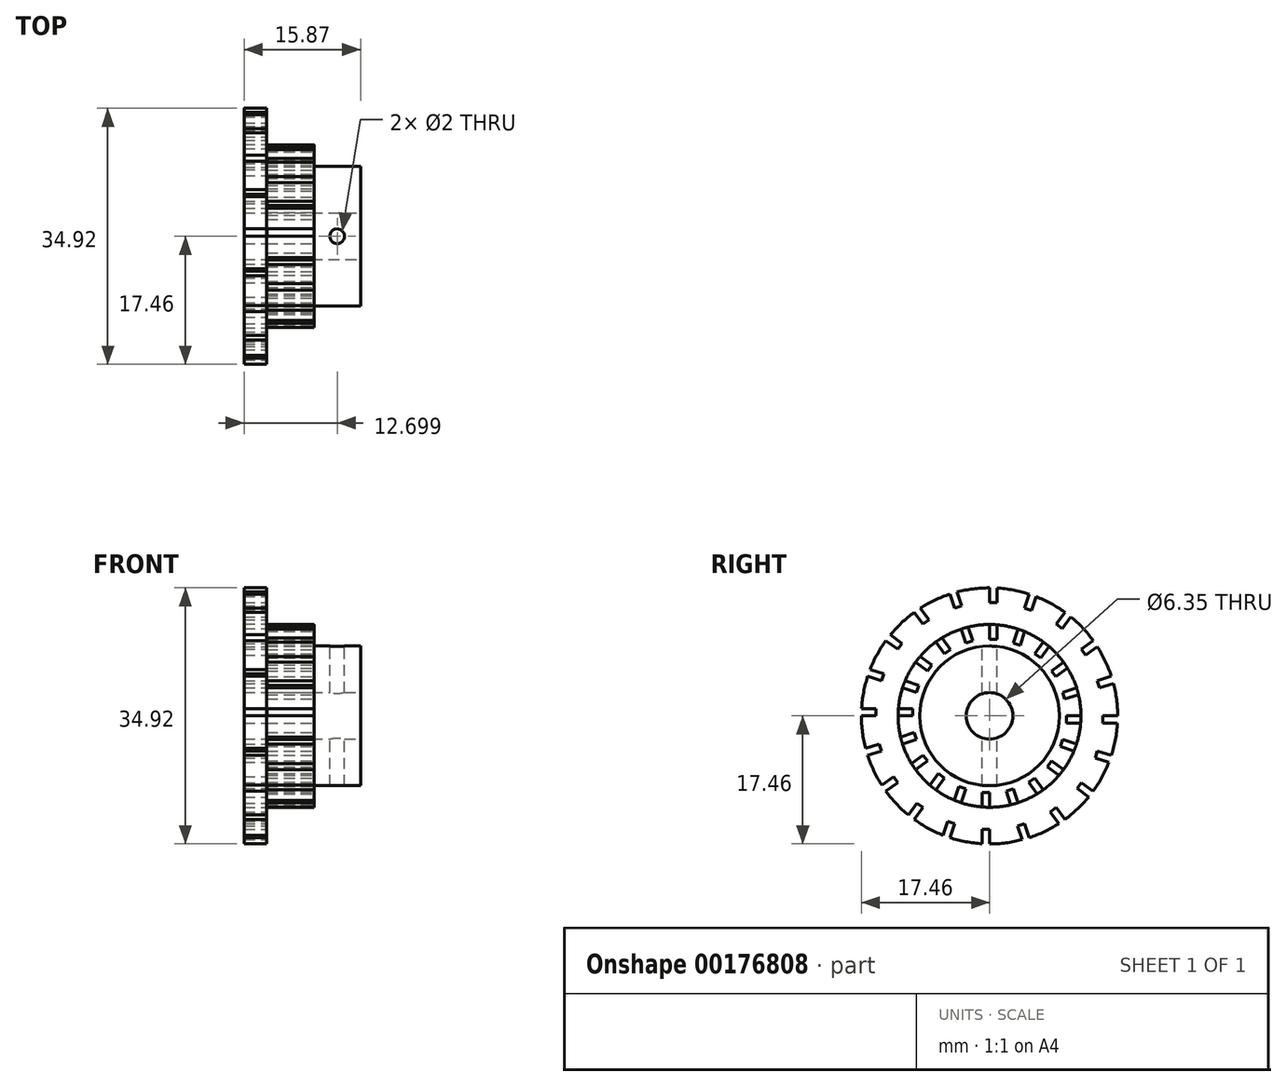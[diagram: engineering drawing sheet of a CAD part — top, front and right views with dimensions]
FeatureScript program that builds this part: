
annotation { "Feature Type Name" : "Feature", "Feature Type Description" : "" }
export const myFeature = defineFeature(function(context is Context, id is Id, definition is map)
    precondition{}
    {
        {
            var Q0;
            Q0=qCreatedBy(makeId("Front.planeOp"),FACE);
            var sketch = newSketch(context, id + "F0", { "sketchPlane" : qUnion([Q0])});
            skLineSegment(sketch, "E0", {"start": v(13.74, 3.18) * mm, "end": v(13.74, 9.53) * mm});
            skLineSegment(sketch, "E1", {"start": v(13.74, 9.53) * mm, "end": v(7.4, 9.53) * mm});
            skLineSegment(sketch, "E2", {"start": v(7.4, 9.53) * mm, "end": v(7.4, 17.46) * mm});
            skLineSegment(sketch, "E3", {"start": v(7.4, 17.46) * mm, "end": v(-2.13, 17.46) * mm});
            skLineSegment(sketch, "E4", {"start": v(-2.13, 17.46) * mm, "end": v(-2.13, 3.18) * mm});
            skLineSegment(sketch, "E5", {"start": v(-2.13, 3.18) * mm, "end": v(13.74, 3.18) * mm});
            skLineSegment(sketch, "E6", {"start": v(4.12, 0) * mm, "end": v(-4.41, 0) * mm, "construction": true});
            skSolve(sketch);
        }
        {
            var Q0;
            Q0=qSketchRegion(id+"F0",true);
            var Q1;
            Q1=sQuery(id+"F0.wireOp",EDGE,"E6");
            revolve(context, id + "F1", {"entities" : qUnion([Q0]), "axis" : qUnion([Q1]), "revolveType" : RevolveType.FULL});
        }
        {
            var Q0;
            Q0=qCreatedBy(makeId("Top.planeOp"),FACE);
            var sketch = newSketch(context, id + "F2", { "sketchPlane" : qUnion([Q0])});
            skLineSegment(sketch, "E7", {"start": v(-2.13, 17.46) * mm, "end": v(7.4, 17.46) * mm});
            skLineSegment(sketch, "E8.0", {"start": v(-2.13, 17.46) * mm, "end": v(-2.13, -17.46) * mm});
            skLineSegment(sketch, "E9.0", {"start": v(7.4, 17.46) * mm, "end": v(7.4, -17.46) * mm});
            skLineSegment(sketch, "E10", {"start": v(0.93, 17.46) * mm, "end": v(0.93, 12.46) * mm});
            skLineSegment(sketch, "E11", {"start": v(0.93, 12.46) * mm, "end": v(7.4, 12.46) * mm});
            skLineSegment(sketch, "E12", {"start": v(7.4, 12.46) * mm, "end": v(7.4, 17.46) * mm});
            skSolve(sketch);
        }
        {
            var Q0;
            Q0=qCreatedBy(makeId("Top.planeOp"),FACE);
            var sketch = newSketch(context, id + "F3", { "sketchPlane" : qUnion([Q0])});
            skLineSegment(sketch, "E13", {"start": v(-2.48, 0) * mm, "end": v(7.78, 0) * mm});
            skSolve(sketch);
        }
        {
            var Q0;
            Q0 = qSketchRegion(id + "F2", true);
            var Q1;
            Q1=sQuery(id+"F3.wireOp",EDGE,"E13");
            revolve(context, id + "F4", {"operationType" : NewBodyOperationType.REMOVE, "entities" : qUnion([Q0]), "axis" : qUnion([Q1]), "revolveType" : RevolveType.FULL, "oppositeDirection" : true});
        }
        {
            var Q0;
            Q0=makeQuery(id+"F4.boolean.opBoolean","COPY",FACE,{"derivedFrom":makeQuery(id+"F4.opRevolve","SWEPT_FACE",FACE,{"disambiguationData":[OSD([sQuery(id+"F2.wireOp",EDGE,"E10")])]})});
            var sketch = newSketch(context, id + "F5", { "sketchPlane" : qUnion([Q0])});
            skLineSegment(sketch, "E14", {"start": v(0, 18.01) * mm, "end": v(0, 15.46) * mm});
            skLineSegment(sketch, "E15", {"start": v(0, 15.46) * mm, "end": v(1, 15.46) * mm});
            skLineSegment(sketch, "E16", {"start": v(1, 15.46) * mm, "end": v(1, 18.04) * mm});
            skLineSegment(sketch, "E17", {"start": v(1, 18.04) * mm, "end": v(0, 18.01) * mm});
            skLineSegment(sketch, "E18.1.0", {"start": v(-4.62, 17.46) * mm, "end": v(-5.57, 17.13) * mm});
            skLineSegment(sketch, "E18.1.1", {"start": v(-3.83, 15.01) * mm, "end": v(-4.62, 17.46) * mm});
            skLineSegment(sketch, "E18.1.2", {"start": v(-5.57, 17.13) * mm, "end": v(-4.78, 14.7) * mm});
            skLineSegment(sketch, "E18.1.3", {"start": v(-4.78, 14.7) * mm, "end": v(-3.83, 15.01) * mm});
            skLineSegment(sketch, "E18.2.0", {"start": v(-9.8, 15.18) * mm, "end": v(-10.59, 14.57) * mm});
            skLineSegment(sketch, "E18.2.1", {"start": v(-8.28, 13.1) * mm, "end": v(-9.8, 15.18) * mm});
            skLineSegment(sketch, "E18.2.2", {"start": v(-10.59, 14.57) * mm, "end": v(-9.09, 12.5) * mm});
            skLineSegment(sketch, "E18.2.3", {"start": v(-9.09, 12.5) * mm, "end": v(-8.28, 13.1) * mm});
            skLineSegment(sketch, "E18.3.0", {"start": v(-14, 11.41) * mm, "end": v(-14.57, 10.59) * mm});
            skLineSegment(sketch, "E18.3.1", {"start": v(-11.92, 9.9) * mm, "end": v(-14, 11.41) * mm});
            skLineSegment(sketch, "E18.3.2", {"start": v(-14.57, 10.59) * mm, "end": v(-12.5, 9.09) * mm});
            skLineSegment(sketch, "E18.3.3", {"start": v(-12.5, 9.09) * mm, "end": v(-11.92, 9.9) * mm});
            skLineSegment(sketch, "E18.4.0", {"start": v(-16.84, 6.52) * mm, "end": v(-17.13, 5.57) * mm});
            skLineSegment(sketch, "E18.4.1", {"start": v(-14.4, 5.73) * mm, "end": v(-16.84, 6.52) * mm});
            skLineSegment(sketch, "E18.4.2", {"start": v(-17.13, 5.57) * mm, "end": v(-14.7, 4.78) * mm});
            skLineSegment(sketch, "E18.4.3", {"start": v(-14.7, 4.78) * mm, "end": v(-14.4, 5.73) * mm});
            skLineSegment(sketch, "E18.5.0", {"start": v(-18.04, 1) * mm, "end": v(-18.01, 0) * mm});
            skLineSegment(sketch, "E18.5.1", {"start": v(-15.46, 1) * mm, "end": v(-18.04, 1) * mm});
            skLineSegment(sketch, "E18.5.2", {"start": v(-18.01, 0) * mm, "end": v(-15.46, 0) * mm});
            skLineSegment(sketch, "E18.5.3", {"start": v(-15.46, 0) * mm, "end": v(-15.46, 1) * mm});
            skLineSegment(sketch, "E18.6.0", {"start": v(-17.46, -4.62) * mm, "end": v(-17.13, -5.57) * mm});
            skLineSegment(sketch, "E18.6.1", {"start": v(-15.01, -3.83) * mm, "end": v(-17.46, -4.62) * mm});
            skLineSegment(sketch, "E18.6.2", {"start": v(-17.13, -5.57) * mm, "end": v(-14.7, -4.78) * mm});
            skLineSegment(sketch, "E18.6.3", {"start": v(-14.7, -4.78) * mm, "end": v(-15.01, -3.83) * mm});
            skLineSegment(sketch, "E18.7.0", {"start": v(-15.18, -9.8) * mm, "end": v(-14.57, -10.59) * mm});
            skLineSegment(sketch, "E18.7.1", {"start": v(-13.1, -8.28) * mm, "end": v(-15.18, -9.8) * mm});
            skLineSegment(sketch, "E18.7.2", {"start": v(-14.57, -10.59) * mm, "end": v(-12.5, -9.09) * mm});
            skLineSegment(sketch, "E18.7.3", {"start": v(-12.5, -9.09) * mm, "end": v(-13.1, -8.28) * mm});
            skLineSegment(sketch, "E18.8.0", {"start": v(-11.41, -14) * mm, "end": v(-10.59, -14.57) * mm});
            skLineSegment(sketch, "E18.8.1", {"start": v(-9.9, -11.92) * mm, "end": v(-11.41, -14) * mm});
            skLineSegment(sketch, "E18.8.2", {"start": v(-10.59, -14.57) * mm, "end": v(-9.09, -12.5) * mm});
            skLineSegment(sketch, "E18.8.3", {"start": v(-9.09, -12.5) * mm, "end": v(-9.9, -11.92) * mm});
            skLineSegment(sketch, "E18.9.0", {"start": v(-6.52, -16.84) * mm, "end": v(-5.57, -17.13) * mm});
            skLineSegment(sketch, "E18.9.1", {"start": v(-5.73, -14.4) * mm, "end": v(-6.52, -16.84) * mm});
            skLineSegment(sketch, "E18.9.2", {"start": v(-5.57, -17.13) * mm, "end": v(-4.78, -14.7) * mm});
            skLineSegment(sketch, "E18.9.3", {"start": v(-4.78, -14.7) * mm, "end": v(-5.73, -14.4) * mm});
            skLineSegment(sketch, "E18.10.0", {"start": v(-1, -18.04) * mm, "end": v(0, -18.01) * mm});
            skLineSegment(sketch, "E18.10.1", {"start": v(-1, -15.46) * mm, "end": v(-1, -18.04) * mm});
            skLineSegment(sketch, "E18.10.2", {"start": v(0, -18.01) * mm, "end": v(0, -15.46) * mm});
            skLineSegment(sketch, "E18.10.3", {"start": v(0, -15.46) * mm, "end": v(-1, -15.46) * mm});
            skLineSegment(sketch, "E18.11.0", {"start": v(4.62, -17.46) * mm, "end": v(5.57, -17.13) * mm});
            skLineSegment(sketch, "E18.11.1", {"start": v(3.83, -15.01) * mm, "end": v(4.62, -17.46) * mm});
            skLineSegment(sketch, "E18.11.2", {"start": v(5.57, -17.13) * mm, "end": v(4.78, -14.7) * mm});
            skLineSegment(sketch, "E18.11.3", {"start": v(4.78, -14.7) * mm, "end": v(3.83, -15.01) * mm});
            skLineSegment(sketch, "E18.12.0", {"start": v(9.8, -15.18) * mm, "end": v(10.59, -14.57) * mm});
            skLineSegment(sketch, "E18.12.1", {"start": v(8.28, -13.1) * mm, "end": v(9.8, -15.18) * mm});
            skLineSegment(sketch, "E18.12.2", {"start": v(10.59, -14.57) * mm, "end": v(9.09, -12.5) * mm});
            skLineSegment(sketch, "E18.12.3", {"start": v(9.09, -12.5) * mm, "end": v(8.28, -13.1) * mm});
            skLineSegment(sketch, "E18.13.0", {"start": v(14, -11.41) * mm, "end": v(14.57, -10.59) * mm});
            skLineSegment(sketch, "E18.13.1", {"start": v(11.92, -9.9) * mm, "end": v(14, -11.41) * mm});
            skLineSegment(sketch, "E18.13.2", {"start": v(14.57, -10.59) * mm, "end": v(12.5, -9.09) * mm});
            skLineSegment(sketch, "E18.13.3", {"start": v(12.5, -9.09) * mm, "end": v(11.92, -9.9) * mm});
            skLineSegment(sketch, "E18.14.0", {"start": v(16.84, -6.52) * mm, "end": v(17.13, -5.57) * mm});
            skLineSegment(sketch, "E18.14.1", {"start": v(14.4, -5.73) * mm, "end": v(16.84, -6.52) * mm});
            skLineSegment(sketch, "E18.14.2", {"start": v(17.13, -5.57) * mm, "end": v(14.7, -4.78) * mm});
            skLineSegment(sketch, "E18.14.3", {"start": v(14.7, -4.78) * mm, "end": v(14.4, -5.73) * mm});
            skLineSegment(sketch, "E18.15.0", {"start": v(18.04, -1) * mm, "end": v(18.01, 0) * mm});
            skLineSegment(sketch, "E18.15.1", {"start": v(15.46, -1) * mm, "end": v(18.04, -1) * mm});
            skLineSegment(sketch, "E18.15.2", {"start": v(18.01, 0) * mm, "end": v(15.46, 0) * mm});
            skLineSegment(sketch, "E18.15.3", {"start": v(15.46, 0) * mm, "end": v(15.46, -1) * mm});
            skLineSegment(sketch, "E18.16.0", {"start": v(17.46, 4.62) * mm, "end": v(17.13, 5.57) * mm});
            skLineSegment(sketch, "E18.16.1", {"start": v(15.01, 3.83) * mm, "end": v(17.46, 4.62) * mm});
            skLineSegment(sketch, "E18.16.2", {"start": v(17.13, 5.57) * mm, "end": v(14.7, 4.78) * mm});
            skLineSegment(sketch, "E18.16.3", {"start": v(14.7, 4.78) * mm, "end": v(15.01, 3.83) * mm});
            skLineSegment(sketch, "E18.17.0", {"start": v(15.18, 9.8) * mm, "end": v(14.57, 10.59) * mm});
            skLineSegment(sketch, "E18.17.1", {"start": v(13.1, 8.28) * mm, "end": v(15.18, 9.8) * mm});
            skLineSegment(sketch, "E18.17.2", {"start": v(14.57, 10.59) * mm, "end": v(12.5, 9.09) * mm});
            skLineSegment(sketch, "E18.17.3", {"start": v(12.5, 9.09) * mm, "end": v(13.1, 8.28) * mm});
            skLineSegment(sketch, "E18.18.0", {"start": v(11.41, 14) * mm, "end": v(10.59, 14.57) * mm});
            skLineSegment(sketch, "E18.18.1", {"start": v(9.9, 11.92) * mm, "end": v(11.41, 14) * mm});
            skLineSegment(sketch, "E18.18.2", {"start": v(10.59, 14.57) * mm, "end": v(9.09, 12.5) * mm});
            skLineSegment(sketch, "E18.18.3", {"start": v(9.09, 12.5) * mm, "end": v(9.9, 11.92) * mm});
            skLineSegment(sketch, "E18.19.0", {"start": v(6.52, 16.84) * mm, "end": v(5.57, 17.13) * mm});
            skLineSegment(sketch, "E18.19.1", {"start": v(5.73, 14.4) * mm, "end": v(6.52, 16.84) * mm});
            skLineSegment(sketch, "E18.19.2", {"start": v(5.57, 17.13) * mm, "end": v(4.78, 14.7) * mm});
            skLineSegment(sketch, "E18.19.3", {"start": v(4.78, 14.7) * mm, "end": v(5.73, 14.4) * mm});
            skPoint(sketch, "E18.center", {"position": v(0, 0) * mm});
            skSolve(sketch);
        }
        {
            var Q0;
            Q0 = qSketchRegion(id + "F5", true);
            extrude(context, id + "F6", {"entities" : qUnion([Q0]), "operationType" : NewBodyOperationType.REMOVE, "oppositeDirection" : true, "depth" : 25 * mm});
        }
        {
            var Q0;
            Q0=makeQuery(id+"F1.opRevolve","SWEPT_FACE",FACE,{"disambiguationData":[OSD([sQuery(id+"F0.wireOp",EDGE,"E2")])]});
            var sketch = newSketch(context, id + "F7", { "sketchPlane" : qUnion([Q0])});
            skLineSegment(sketch, "E19", {"start": v(0, 12.86) * mm, "end": v(0, 10.46) * mm});
            skLineSegment(sketch, "E20", {"start": v(0, 10.46) * mm, "end": v(1, 10.46) * mm});
            skLineSegment(sketch, "E21", {"start": v(1, 10.46) * mm, "end": v(1, 12.93) * mm});
            skLineSegment(sketch, "E22", {"start": v(1, 12.93) * mm, "end": v(0, 12.86) * mm});
            skLineSegment(sketch, "E23.1.0", {"start": v(-3.05, 12.6) * mm, "end": v(-3.97, 12.23) * mm});
            skLineSegment(sketch, "E23.1.1", {"start": v(-2.28, 10.26) * mm, "end": v(-3.05, 12.6) * mm});
            skLineSegment(sketch, "E23.1.2", {"start": v(-3.97, 12.23) * mm, "end": v(-3.23, 9.95) * mm});
            skLineSegment(sketch, "E23.1.3", {"start": v(-3.23, 9.95) * mm, "end": v(-2.28, 10.26) * mm});
            skLineSegment(sketch, "E23.2.0", {"start": v(-6.8, 11.05) * mm, "end": v(-7.56, 10.4) * mm});
            skLineSegment(sketch, "E23.2.1", {"start": v(-5.34, 9.05) * mm, "end": v(-6.8, 11.05) * mm});
            skLineSegment(sketch, "E23.2.2", {"start": v(-7.56, 10.4) * mm, "end": v(-6.15, 8.46) * mm});
            skLineSegment(sketch, "E23.2.3", {"start": v(-6.15, 8.46) * mm, "end": v(-5.34, 9.05) * mm});
            skPoint(sketch, "E23.center", {"position": v(0, 0) * mm});
            skLineSegment(sketch, "E24.2.3.0", {"start": v(-9.88, 8.41) * mm, "end": v(-10.4, 7.56) * mm});
            skLineSegment(sketch, "E24.3.3.0", {"start": v(-7.88, 6.96) * mm, "end": v(-9.88, 8.41) * mm});
            skLineSegment(sketch, "E24.6.3.0", {"start": v(-10.4, 7.56) * mm, "end": v(-8.46, 6.15) * mm});
            skLineSegment(sketch, "E24.9.3.0", {"start": v(-8.46, 6.15) * mm, "end": v(-7.88, 6.96) * mm});
            skLineSegment(sketch, "E24.2.4.0", {"start": v(-12, 4.95) * mm, "end": v(-12.23, 3.97) * mm});
            skLineSegment(sketch, "E24.3.4.0", {"start": v(-9.64, 4.18) * mm, "end": v(-12, 4.95) * mm});
            skLineSegment(sketch, "E24.6.4.0", {"start": v(-12.23, 3.97) * mm, "end": v(-9.95, 3.23) * mm});
            skLineSegment(sketch, "E24.9.4.0", {"start": v(-9.95, 3.23) * mm, "end": v(-9.64, 4.18) * mm});
            skLineSegment(sketch, "E24.2.5.0", {"start": v(-12.93, 1) * mm, "end": v(-12.86, 0) * mm});
            skLineSegment(sketch, "E24.3.5.0", {"start": v(-10.46, 1) * mm, "end": v(-12.93, 1) * mm});
            skLineSegment(sketch, "E24.6.5.0", {"start": v(-12.86, 0) * mm, "end": v(-10.46, 0) * mm});
            skLineSegment(sketch, "E24.9.5.0", {"start": v(-10.46, 0) * mm, "end": v(-10.46, 1) * mm});
            skLineSegment(sketch, "E24.2.6.0", {"start": v(-12.6, -3.05) * mm, "end": v(-12.23, -3.97) * mm});
            skLineSegment(sketch, "E24.3.6.0", {"start": v(-10.26, -2.28) * mm, "end": v(-12.6, -3.05) * mm});
            skLineSegment(sketch, "E24.6.6.0", {"start": v(-12.23, -3.97) * mm, "end": v(-9.95, -3.23) * mm});
            skLineSegment(sketch, "E24.9.6.0", {"start": v(-9.95, -3.23) * mm, "end": v(-10.26, -2.28) * mm});
            skLineSegment(sketch, "E24.2.7.0", {"start": v(-11.05, -6.8) * mm, "end": v(-10.4, -7.56) * mm});
            skLineSegment(sketch, "E24.3.7.0", {"start": v(-9.05, -5.34) * mm, "end": v(-11.05, -6.8) * mm});
            skLineSegment(sketch, "E24.6.7.0", {"start": v(-10.4, -7.56) * mm, "end": v(-8.46, -6.15) * mm});
            skLineSegment(sketch, "E24.9.7.0", {"start": v(-8.46, -6.15) * mm, "end": v(-9.05, -5.34) * mm});
            skLineSegment(sketch, "E24.2.8.0", {"start": v(-8.41, -9.88) * mm, "end": v(-7.56, -10.4) * mm});
            skLineSegment(sketch, "E24.3.8.0", {"start": v(-6.96, -7.88) * mm, "end": v(-8.41, -9.88) * mm});
            skLineSegment(sketch, "E24.6.8.0", {"start": v(-7.56, -10.4) * mm, "end": v(-6.15, -8.46) * mm});
            skLineSegment(sketch, "E24.9.8.0", {"start": v(-6.15, -8.46) * mm, "end": v(-6.96, -7.88) * mm});
            skLineSegment(sketch, "E24.2.9.0", {"start": v(-4.95, -12) * mm, "end": v(-3.97, -12.23) * mm});
            skLineSegment(sketch, "E24.3.9.0", {"start": v(-4.18, -9.64) * mm, "end": v(-4.95, -12) * mm});
            skLineSegment(sketch, "E24.6.9.0", {"start": v(-3.97, -12.23) * mm, "end": v(-3.23, -9.95) * mm});
            skLineSegment(sketch, "E24.9.9.0", {"start": v(-3.23, -9.95) * mm, "end": v(-4.18, -9.64) * mm});
            skLineSegment(sketch, "E24.2.10.0", {"start": v(-1, -12.93) * mm, "end": v(0, -12.86) * mm});
            skLineSegment(sketch, "E24.3.10.0", {"start": v(-1, -10.46) * mm, "end": v(-1, -12.93) * mm});
            skLineSegment(sketch, "E24.6.10.0", {"start": v(0, -12.86) * mm, "end": v(0, -10.46) * mm});
            skLineSegment(sketch, "E24.9.10.0", {"start": v(0, -10.46) * mm, "end": v(-1, -10.46) * mm});
            skLineSegment(sketch, "E24.2.11.0", {"start": v(3.05, -12.6) * mm, "end": v(3.97, -12.23) * mm});
            skLineSegment(sketch, "E24.3.11.0", {"start": v(2.28, -10.26) * mm, "end": v(3.05, -12.6) * mm});
            skLineSegment(sketch, "E24.6.11.0", {"start": v(3.97, -12.23) * mm, "end": v(3.23, -9.95) * mm});
            skLineSegment(sketch, "E24.9.11.0", {"start": v(3.23, -9.95) * mm, "end": v(2.28, -10.26) * mm});
            skLineSegment(sketch, "E24.2.12.0", {"start": v(6.8, -11.05) * mm, "end": v(7.56, -10.4) * mm});
            skLineSegment(sketch, "E24.3.12.0", {"start": v(5.34, -9.05) * mm, "end": v(6.8, -11.05) * mm});
            skLineSegment(sketch, "E24.6.12.0", {"start": v(7.56, -10.4) * mm, "end": v(6.15, -8.46) * mm});
            skLineSegment(sketch, "E24.9.12.0", {"start": v(6.15, -8.46) * mm, "end": v(5.34, -9.05) * mm});
            skLineSegment(sketch, "E24.2.13.0", {"start": v(9.88, -8.41) * mm, "end": v(10.4, -7.56) * mm});
            skLineSegment(sketch, "E24.3.13.0", {"start": v(7.88, -6.96) * mm, "end": v(9.88, -8.41) * mm});
            skLineSegment(sketch, "E24.6.13.0", {"start": v(10.4, -7.56) * mm, "end": v(8.46, -6.15) * mm});
            skLineSegment(sketch, "E24.9.13.0", {"start": v(8.46, -6.15) * mm, "end": v(7.88, -6.96) * mm});
            skLineSegment(sketch, "E24.2.14.0", {"start": v(12, -4.95) * mm, "end": v(12.23, -3.97) * mm});
            skLineSegment(sketch, "E24.3.14.0", {"start": v(9.64, -4.18) * mm, "end": v(12, -4.95) * mm});
            skLineSegment(sketch, "E24.6.14.0", {"start": v(12.23, -3.97) * mm, "end": v(9.95, -3.23) * mm});
            skLineSegment(sketch, "E24.9.14.0", {"start": v(9.95, -3.23) * mm, "end": v(9.64, -4.18) * mm});
            skLineSegment(sketch, "E24.2.15.0", {"start": v(12.93, -1) * mm, "end": v(12.86, 0) * mm});
            skLineSegment(sketch, "E24.3.15.0", {"start": v(10.46, -1) * mm, "end": v(12.93, -1) * mm});
            skLineSegment(sketch, "E24.6.15.0", {"start": v(12.86, 0) * mm, "end": v(10.46, 0) * mm});
            skLineSegment(sketch, "E24.9.15.0", {"start": v(10.46, 0) * mm, "end": v(10.46, -1) * mm});
            skLineSegment(sketch, "E24.2.16.0", {"start": v(12.6, 3.05) * mm, "end": v(12.23, 3.97) * mm});
            skLineSegment(sketch, "E24.3.16.0", {"start": v(10.26, 2.28) * mm, "end": v(12.6, 3.05) * mm});
            skLineSegment(sketch, "E24.6.16.0", {"start": v(12.23, 3.97) * mm, "end": v(9.95, 3.23) * mm});
            skLineSegment(sketch, "E24.9.16.0", {"start": v(9.95, 3.23) * mm, "end": v(10.26, 2.28) * mm});
            skLineSegment(sketch, "E24.2.17.0", {"start": v(11.05, 6.8) * mm, "end": v(10.4, 7.56) * mm});
            skLineSegment(sketch, "E24.3.17.0", {"start": v(9.05, 5.34) * mm, "end": v(11.05, 6.8) * mm});
            skLineSegment(sketch, "E24.6.17.0", {"start": v(10.4, 7.56) * mm, "end": v(8.46, 6.15) * mm});
            skLineSegment(sketch, "E24.9.17.0", {"start": v(8.46, 6.15) * mm, "end": v(9.05, 5.34) * mm});
            skLineSegment(sketch, "E24.2.18.0", {"start": v(8.41, 9.88) * mm, "end": v(7.56, 10.4) * mm});
            skLineSegment(sketch, "E24.3.18.0", {"start": v(6.96, 7.88) * mm, "end": v(8.41, 9.88) * mm});
            skLineSegment(sketch, "E24.6.18.0", {"start": v(7.56, 10.4) * mm, "end": v(6.15, 8.46) * mm});
            skLineSegment(sketch, "E24.9.18.0", {"start": v(6.15, 8.46) * mm, "end": v(6.96, 7.88) * mm});
            skLineSegment(sketch, "E24.2.19.0", {"start": v(4.95, 12) * mm, "end": v(3.97, 12.23) * mm});
            skLineSegment(sketch, "E24.3.19.0", {"start": v(4.18, 9.64) * mm, "end": v(4.95, 12) * mm});
            skLineSegment(sketch, "E24.6.19.0", {"start": v(3.97, 12.23) * mm, "end": v(3.23, 9.95) * mm});
            skLineSegment(sketch, "E24.9.19.0", {"start": v(3.23, 9.95) * mm, "end": v(4.18, 9.64) * mm});
            skSolve(sketch);
        }
        {
            var Q0;
            Q0 = qSketchRegion(id + "F7", true);
            extrude(context, id + "F8", {"entities" : qUnion([Q0]), "operationType" : NewBodyOperationType.REMOVE, "oppositeDirection" : true, "depth" : 6.4 * mm});
        }
        {
            var Q0;
            Q0=qCreatedBy(makeId("Top.planeOp"),FACE);
            var sketch = newSketch(context, id + "F9", { "sketchPlane" : qUnion([Q0])});
            skLineSegment(sketch, "E25", {"start": v(7.4, 9.53) * mm, "end": v(13.74, 9.53) * mm});
            skLineSegment(sketch, "E26.0", {"start": v(13.74, 9.53) * mm, "end": v(13.74, -9.53) * mm});
            skLineSegment(sketch, "E27", {"start": v(13.74, -9.53) * mm, "end": v(7.4, -9.53) * mm});
            skCircle(sketch, "E28", {"center": v(10.57, 0) * mm, "radius": 1 * mm});
            skPoint(sketch, "E28.centerSnap0", {"position": v(10.57, 9.53) * mm});
            skSolve(sketch);
        }
        {
            var Q0;
            Q0 = qSketchRegion(id + "F9", true);
            extrude(context, id + "F10", {"entities" : qUnion([Q0]), "operationType" : NewBodyOperationType.REMOVE, "oppositeDirection" : true, "depth" : 25 * mm, "hasSecondDirection" : true, "secondDirectionOppositeDirection" : false, "secondDirectionDepth" : 25 * mm});
        }
    });
